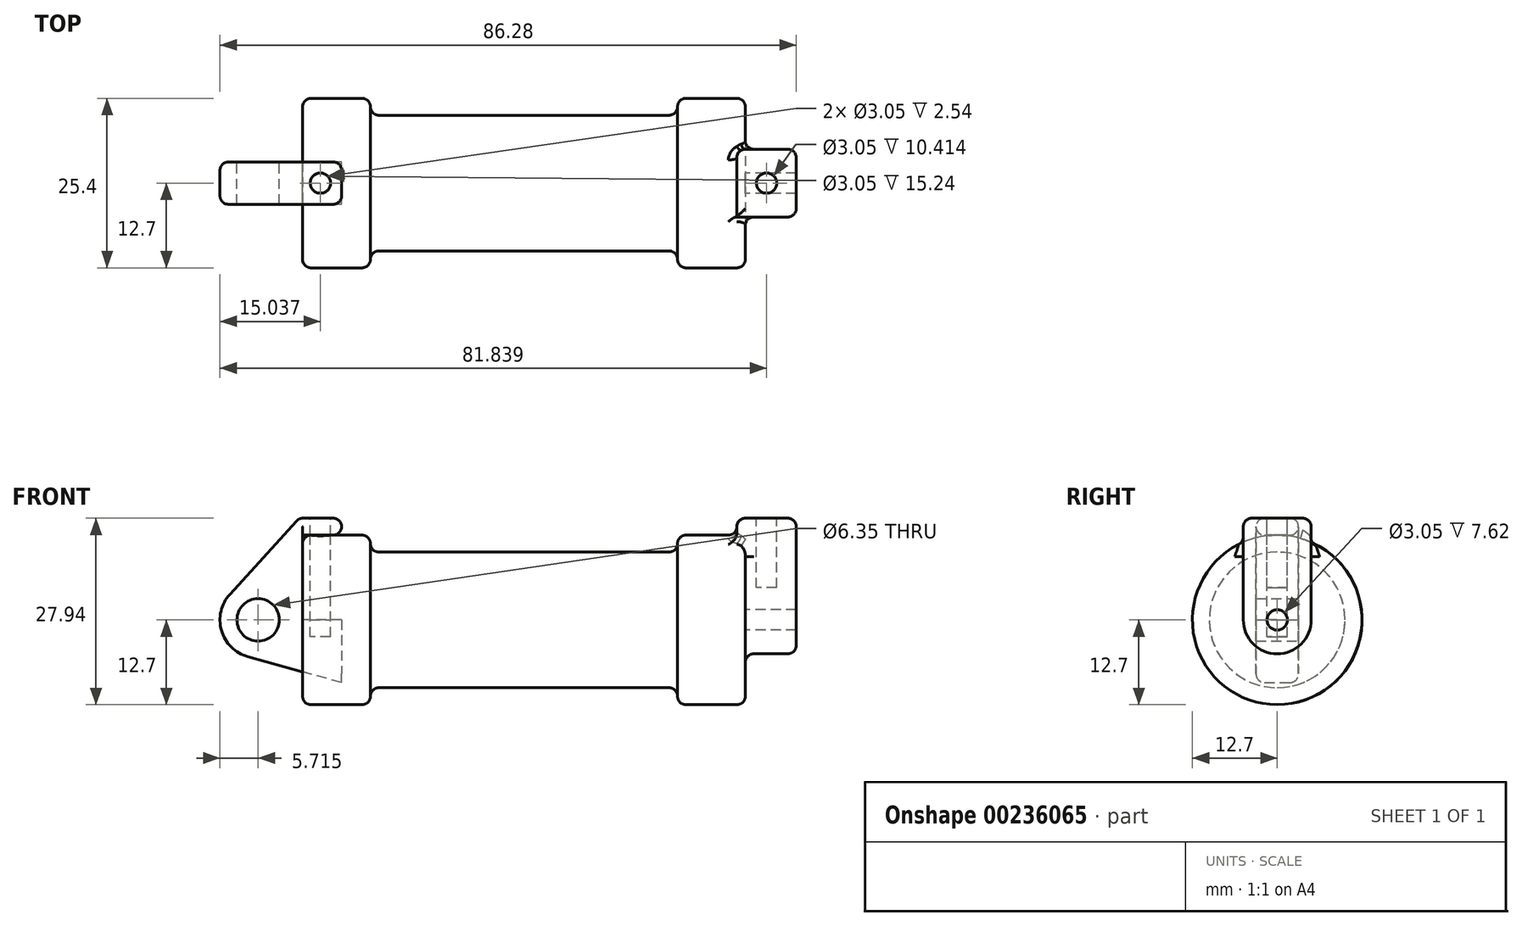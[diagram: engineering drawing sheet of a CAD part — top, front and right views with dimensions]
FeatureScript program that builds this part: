
annotation { "Feature Type Name" : "Feature", "Feature Type Description" : "" }
export const myFeature = defineFeature(function(context is Context, id is Id, definition is map)
    precondition{}
    {
        {
            var Q0;
            Q0=qCreatedBy(makeId("Front.planeOp"),FACE);
            var sketch = newSketch(context, id + "F0", { "sketchPlane" : qUnion([Q0])});
            skLineSegment(sketch, "E0", {"start": v(0, 0) * mm, "end": v(0, 12.7) * mm});
            skLineSegment(sketch, "E1", {"start": v(0, 12.7) * mm, "end": v(10.16, 12.7) * mm});
            skLineSegment(sketch, "E2", {"start": v(10.16, 12.7) * mm, "end": v(10.16, 10.16) * mm});
            skLineSegment(sketch, "E3", {"start": v(10.16, 10.16) * mm, "end": v(56.13, 10.16) * mm});
            skLineSegment(sketch, "E4", {"start": v(56.13, 10.16) * mm, "end": v(56.13, 12.7) * mm});
            skLineSegment(sketch, "E5", {"start": v(56.13, 12.7) * mm, "end": v(66.3, 12.7) * mm});
            skLineSegment(sketch, "E6", {"start": v(66.3, 12.7) * mm, "end": v(66.3, 0) * mm});
            skLineSegment(sketch, "E7", {"start": v(66.3, 0) * mm, "end": v(0, 0) * mm});
            skLineSegment(sketch, "E8", {"start": v(5.84, 15.24) * mm, "end": v(-0.5, 15.24) * mm});
            skLineSegment(sketch, "E9", {"start": v(-0.5, 15.24) * mm, "end": v(-10.88, 3.85) * mm});
            skLineSegment(sketch, "E10", {"start": v(0, 0) * mm, "end": v(-6.65, 0) * mm});
            skCircle(sketch, "E11", {"center": v(-6.65, 0) * mm, "radius": 5.72 * mm});
            skCircle(sketch, "E12", {"center": v(-6.65, 0) * mm, "radius": 3.18 * mm});
            skLineSegment(sketch, "E13", {"start": v(5.84, 15.24) * mm, "end": v(5.84, -9.4) * mm});
            skLineSegment(sketch, "E14", {"start": v(5.84, -9.4) * mm, "end": v(-8.18, -5.5) * mm});
            skSolve(sketch);
        }
        {
            var Q0;
            {var subQ0=sQuery(id+"F0.wireOp",EDGE,"E2");Q0=makeQuery(id+"F0.imprint","IMPRINT",FACE,{"disambiguationData":[TD([[makeQuery(id+"F0.imprint","IMPRINT",EDGE,{"derivedFrom":subQ0}),-1.0]])]});}
            var Q1;
            {var subQ0=sQuery(id+"F0.wireOp",EDGE,"E0");Q1=makeQuery(id+"F0.imprint","IMPRINT",FACE,{"disambiguationData":[TD([[makeQuery(id+"F0.imprint","IMPRINT",EDGE,{"derivedFrom":subQ0}),-1.0]])]});}
            var Q2;
            Q2=sQuery(id+"F0.wireOp",EDGE,"E7");
            revolve(context, id + "F1", {"entities" : qUnion([Q0, Q1]), "axis" : qUnion([Q2]), "revolveType" : RevolveType.FULL});
        }
        {
            var Q0;
            {var subQ3=sQuery(id+"F0.wireOp",EDGE,"E0");Q0=makeQuery(id+"F0.imprint","IMPRINT",FACE,{"disambiguationData":[TD([[makeQuery(id+"F0.imprint","IMPRINT",EDGE,{"derivedFrom":subQ3}),1.0]])]});}
            var Q1;
            {var subQ0=sQuery(id+"F0.wireOp",EDGE,"E14");Q1=makeQuery(id+"F0.imprint","IMPRINT",FACE,{"disambiguationData":[TD([[makeQuery(id+"F0.imprint","IMPRINT",EDGE,{"derivedFrom":subQ0}),-1.0]])]});}
            var Q2;
            {var subQ4=sQuery(id+"F0.wireOp",EDGE,"E12");Q2=makeQuery(id+"F0.imprint","IMPRINT",FACE,{"disambiguationData":[TD([[makeQuery(id+"F0.imprint","IMPRINT",EDGE,{"derivedFrom":subQ4}),-1.0]])]});}
            extrude(context, id + "F2", {"entities" : qUnion([Q0, Q1, Q2]), "endBound" : BoundingType.SYMMETRIC, "depth" : 6.35 * mm});
        }
        {
            var Q0;
            {var subQ0=sQuery(id+"F0.wireOp",EDGE,"E6");Q0=makeQuery(id+"F2.boolean.opBoolean","MERGE",FACE,{"derivedFrom":[makeQuery(id+"F1.opRevolve","SWEPT_FACE",FACE,{"disambiguationData":[OSD([subQ0])]}),makeQuery(id+"F2.opExtrude","SWEPT_FACE",FACE,{"disambiguationData":[OSD([subQ0])]})]});}
            var sketch = newSketch(context, id + "F3", { "sketchPlane" : qUnion([Q0])});
            skCircle(sketch, "E15", {"center": v(0, 0) * mm, "radius": 1.52 * mm});
            skCircle(sketch, "E16", {"center": v(0, 0) * mm, "radius": 5.08 * mm});
            skLineSegment(sketch, "E17", {"start": v(-5.08, 0) * mm, "end": v(-5.08, 15.24) * mm});
            skLineSegment(sketch, "E18", {"start": v(5.08, 0) * mm, "end": v(5.08, 15.24) * mm});
            skLineSegment(sketch, "E19", {"start": v(5.08, 15.24) * mm, "end": v(-5.08, 15.24) * mm});
            skSolve(sketch);
        }
        {
            var Q0;
            {var subQ0=sQuery(id+"F3.wireOp",EDGE,"E19");Q0=makeQuery(id+"F3.imprint","IMPRINT",FACE,{"disambiguationData":[TD([[makeQuery(id+"F3.imprint","IMPRINT",EDGE,{"derivedFrom":subQ0}),1.0]])]});}
            var Q1;
            {var subQ0=sQuery(id+"F0.wireOp",EDGE,"E6");var subQ10=makeQuery(id+"F2.opExtrude","CAP_EDGE",EDGE,{"disambiguationData":[OSD([subQ0])],"isStart":true});Q1=makeQuery(id+"F3.imprint","IMPRINT",FACE,{"disambiguationData":[TD([[makeQuery(id+"F3.imprint","IMPRINT",EDGE,{"derivedFrom":subQ10}),-1.0]])]});}
            var Q2;
            Q2=makeQuery(id+"F3.imprint","IMPRINT",FACE,{"disambiguationData":[TD([[makeQuery(id+"F3.imprint","IMPRINT",EDGE,{"derivedFrom":sQuery(id+"F3.wireOp",EDGE,"E15")}),-1.0]])]});
            var Q3;
            {var subQ0=sQuery(id+"F3.wireOp",EDGE,"E17");var subQ1=sQuery(id+"F3.wireOp",EDGE,"E16");var subQ2=makeQuery(id+"F3.imprint","INTERSECT",VERTEX,{"derivedFrom":[subQ1,subQ0]});Q3=makeQuery(id+"F3.imprint","IMPRINT",FACE,{"disambiguationData":[TD([[makeQuery(id+"F3.imprint","IMPRINT",EDGE,{"disambiguationData":[TD([[subQ2,1.0]])],"derivedFrom":subQ1}),-1.0]])]});}
            extrude(context, id + "F4", {"entities" : qUnion([Q0, Q1, Q2, Q3]), "operationType" : NewBodyOperationType.ADD, "depth" : 7.62 * mm, "hasSecondDirection" : true, "secondDirectionOppositeDirection" : true, "secondDirectionDepth" : 1.27 * mm});
        }
        {
            var Q0;
            Q0=makeQuery(id+"F4.opExtrude","SWEPT_FACE",FACE,{"disambiguationData":[OSD([sQuery(id+"F3.wireOp",EDGE,"E19")])]});
            var sketch = newSketch(context, id + "F5", { "sketchPlane" : qUnion([Q0])});
            skCircle(sketch, "E20", {"center": v(69.47, 0) * mm, "radius": 1.52 * mm});
            skSolve(sketch);
        }
        {
            var Q0;
            Q0=makeQuery(id+"F5.imprint","IMPRINT",FACE,{"disambiguationData":[TD([[makeQuery(id+"F5.imprint","IMPRINT",EDGE,{"derivedFrom":sQuery(id+"F5.wireOp",EDGE,"E20")}),1.0]])]});
            extrude(context, id + "F6", {"entities" : qUnion([Q0]), "operationType" : NewBodyOperationType.REMOVE, "oppositeDirection" : true, "depth" : 10.4 * mm});
        }
        {
            var Q0;
            Q0=makeQuery(id+"F2.opExtrude","SWEPT_FACE",FACE,{"disambiguationData":[OSD([sQuery(id+"F0.wireOp",EDGE,"E8")])]});
            var sketch = newSketch(context, id + "F7", { "sketchPlane" : qUnion([Q0])});
            skCircle(sketch, "E21", {"center": v(2.67, 0) * mm, "radius": 1.52 * mm});
            skSolve(sketch);
        }
        {
            var Q0;
            Q0=makeQuery(id+"F7.imprint","IMPRINT",FACE,{"disambiguationData":[TD([[makeQuery(id+"F7.imprint","IMPRINT",EDGE,{"derivedFrom":sQuery(id+"F7.wireOp",EDGE,"E21")}),1.0]])]});
            extrude(context, id + "F8", {"entities" : qUnion([Q0]), "operationType" : NewBodyOperationType.REMOVE, "oppositeDirection" : true, "depth" : 17.78 * mm});
        }
        {
            var Q0;
            Q0=makeQuery(id+"F1.opRevolve","SWEPT_EDGE",EDGE,{"disambiguationData":[OSD([sQuery(id+"F0.wireOp",EDGE,"E1"),sQuery(id+"F0.wireOp",EDGE,"E2")])]});
            fillet(context, id + "F9", {"entities" : qUnion([Q0]), "radius" : 1.27 * mm, "tangentPropagation" : true, "allowEdgeOverflow" : false});
        }
        {
            var Q0;
            Q0=makeQuery(id+"F1.opRevolve","SWEPT_EDGE",EDGE,{"disambiguationData":[OSD([sQuery(id+"F0.wireOp",EDGE,"E0"),sQuery(id+"F0.wireOp",EDGE,"E1")])]});
            fillet(context, id + "F10", {"entities" : qUnion([Q0]), "radius" : 1.27 * mm, "tangentPropagation" : true, "allowEdgeOverflow" : false});
        }
        {
            var Q0;
            Q0=makeQuery(id+"F2.opExtrude","SWEPT_EDGE",EDGE,{"disambiguationData":[OSD([sQuery(id+"F0.wireOp",EDGE,"E8"),sQuery(id+"F0.wireOp",EDGE,"E9")])]});
            fillet(context, id + "F11", {"entities" : qUnion([Q0]), "radius" : 1.27 * mm, "tangentPropagation" : true, "allowEdgeOverflow" : false});
        }
        {
            var Q0;
            Q0=makeQuery(id+"F2.opExtrude","CAP_EDGE",EDGE,{"disambiguationData":[OSD([sQuery(id+"F0.wireOp",EDGE,"E8")])],"isStart":false});
            fillet(context, id + "F12", {"entities" : qUnion([Q0]), "radius" : 1.27 * mm, "tangentPropagation" : true, "allowEdgeOverflow" : false});
        }
        {
            var Q0;
            Q0=makeQuery(id+"F2.opExtrude","SWEPT_EDGE",EDGE,{"disambiguationData":[OSD([sQuery(id+"F0.wireOp",EDGE,"E8"),sQuery(id+"F0.wireOp",EDGE,"E13")])]});
            fillet(context, id + "F13", {"entities" : qUnion([Q0]), "radius" : 1.27 * mm, "tangentPropagation" : true, "allowEdgeOverflow" : false});
        }
        {
            var Q0;
            Q0=makeQuery(id+"F2.opExtrude","CAP_EDGE",EDGE,{"disambiguationData":[OSD([sQuery(id+"F0.wireOp",EDGE,"E8")])],"isStart":true});
            fillet(context, id + "F14", {"entities" : qUnion([Q0]), "radius" : 1.27 * mm, "tangentPropagation" : true, "allowEdgeOverflow" : false});
        }
        {
            var Q0;
            Q0=makeQuery(id+"F4.opExtrude","SWEPT_EDGE",EDGE,{"disambiguationData":[OSD([sQuery(id+"F3.wireOp",EDGE,"E18"),sQuery(id+"F3.wireOp",EDGE,"E19")])]});
            fillet(context, id + "F15", {"entities" : qUnion([Q0]), "radius" : 1.27 * mm, "tangentPropagation" : true, "allowEdgeOverflow" : false});
        }
        {
            var Q0;
            Q0=makeQuery(id+"F4.opExtrude","CAP_EDGE",EDGE,{"disambiguationData":[OSD([sQuery(id+"F3.wireOp",EDGE,"E19")])],"isStart":false});
            var Q1;
            Q1=makeQuery(id+"F4.opExtrude","SWEPT_EDGE",EDGE,{"disambiguationData":[OSD([sQuery(id+"F3.wireOp",EDGE,"E17"),sQuery(id+"F3.wireOp",EDGE,"E19")])]});
            var Q2;
            Q2=makeQuery(id+"F4.opExtrude","CAP_EDGE",EDGE,{"disambiguationData":[OSD([sQuery(id+"F3.wireOp",EDGE,"E19")])],"isStart":true});
            fillet(context, id + "F16", {"entities" : qUnion([Q0, Q1, Q2]), "radius" : 1.27 * mm, "tangentPropagation" : true, "allowEdgeOverflow" : false});
        }
        {
            var Q0;
            Q0=makeQuery(id+"F1.opRevolve","SWEPT_EDGE",EDGE,{"disambiguationData":[OSD([sQuery(id+"F0.wireOp",EDGE,"E4"),sQuery(id+"F0.wireOp",EDGE,"E5")])]});
            var Q1;
            Q1=makeQuery(id+"F1.opRevolve","SWEPT_EDGE",EDGE,{"disambiguationData":[OSD([sQuery(id+"F0.wireOp",EDGE,"E5"),sQuery(id+"F0.wireOp",EDGE,"E6")])]});
            fillet(context, id + "F17", {"entities" : qUnion([Q0, Q1]), "radius" : 1.27 * mm, "tangentPropagation" : true, "allowEdgeOverflow" : false});
        }
        {
            var Q0;
            Q0=makeQuery(id+"F4.boolean.opBoolean","INTERSECT",EDGE,{"derivedFrom":[makeQuery(id+"F1.opRevolve","SWEPT_FACE",FACE,{"disambiguationData":[OSD([sQuery(id+"F0.wireOp",EDGE,"E6")])]}),makeQuery(id+"F4.opExtrude","SWEPT_FACE",FACE,{"disambiguationData":[OSD([sQuery(id+"F3.wireOp",EDGE,"E17")])]})]});
            fillet(context, id + "F18", {"entities" : qUnion([Q0]), "radius" : 1.27 * mm, "tangentPropagation" : true, "allowEdgeOverflow" : false});
        }
        {
            var Q0;
            Q0=makeQuery(id+"F2.opExtrude","CAP_EDGE",EDGE,{"disambiguationData":[OSD([sQuery(id+"F0.wireOp",EDGE,"E1")])],"isStart":true});
            fillet(context, id + "F19", {"entities" : qUnion([Q0]), "radius" : 1.27 * mm, "tangentPropagation" : true, "allowEdgeOverflow" : false});
        }
        {
            var Q0;
            Q0=makeQuery(id+"F1.opRevolve","SWEPT_EDGE",EDGE,{"disambiguationData":[OSD([sQuery(id+"F0.wireOp",EDGE,"E3"),sQuery(id+"F0.wireOp",EDGE,"E4")])]});
            fillet(context, id + "F20", {"entities" : qUnion([Q0]), "radius" : 1.27 * mm, "tangentPropagation" : true, "allowEdgeOverflow" : false});
        }
        {
            var Q0;
            Q0=makeQuery(id+"F1.opRevolve","SWEPT_EDGE",EDGE,{"disambiguationData":[OSD([sQuery(id+"F0.wireOp",EDGE,"E2"),sQuery(id+"F0.wireOp",EDGE,"E3")])]});
            fillet(context, id + "F21", {"entities" : qUnion([Q0]), "radius" : 1.27 * mm, "tangentPropagation" : true, "allowEdgeOverflow" : false});
        }
    });
